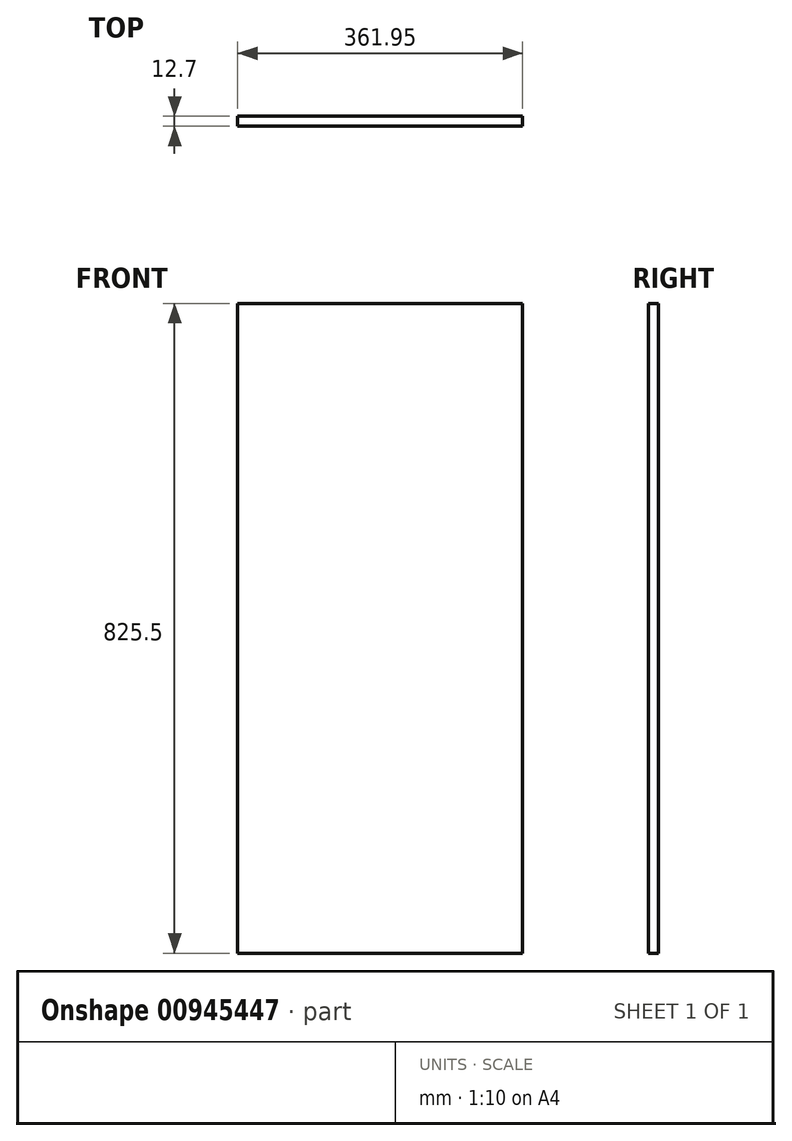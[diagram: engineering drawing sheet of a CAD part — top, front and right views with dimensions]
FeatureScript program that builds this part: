
annotation { "Feature Type Name" : "Feature", "Feature Type Description" : "" }
export const myFeature = defineFeature(function(context is Context, id is Id, definition is map)
    precondition{}
    {
        {
            var Q0;
            Q0=qCreatedBy(makeId("Front.planeOp"),FACE);
            var sketch = newSketch(context, id + "F0", { "sketchPlane" : qUnion([Q0])});
            skLineSegment(sketch, "E0.bottom", {"start": v(0, 0) * mm, "end": v(361.95, 0) * mm});
            skLineSegment(sketch, "E0.top", {"start": v(0, 825.5) * mm, "end": v(361.95, 825.5) * mm});
            skLineSegment(sketch, "E0.left", {"start": v(0, 0) * mm, "end": v(0, 825.5) * mm});
            skLineSegment(sketch, "E0.right", {"start": v(361.95, 0) * mm, "end": v(361.95, 825.5) * mm});
            skSolve(sketch);
        }
        {
            var Q0;
            Q0=makeQuery(id+"F0.imprint","IMPRINT",FACE,{"disambiguationData":[TD([[makeQuery(id+"F0.imprint","IMPRINT",EDGE,{"derivedFrom":sQuery(id+"F0.wireOp",EDGE,"E0.bottom")}),1.0]])]});
            extrude(context, id + "F1", {"entities" : qUnion([Q0]), "depth" : 12.7 * mm, "offsetDistance" : 25.4 * mm});
        }
    });
